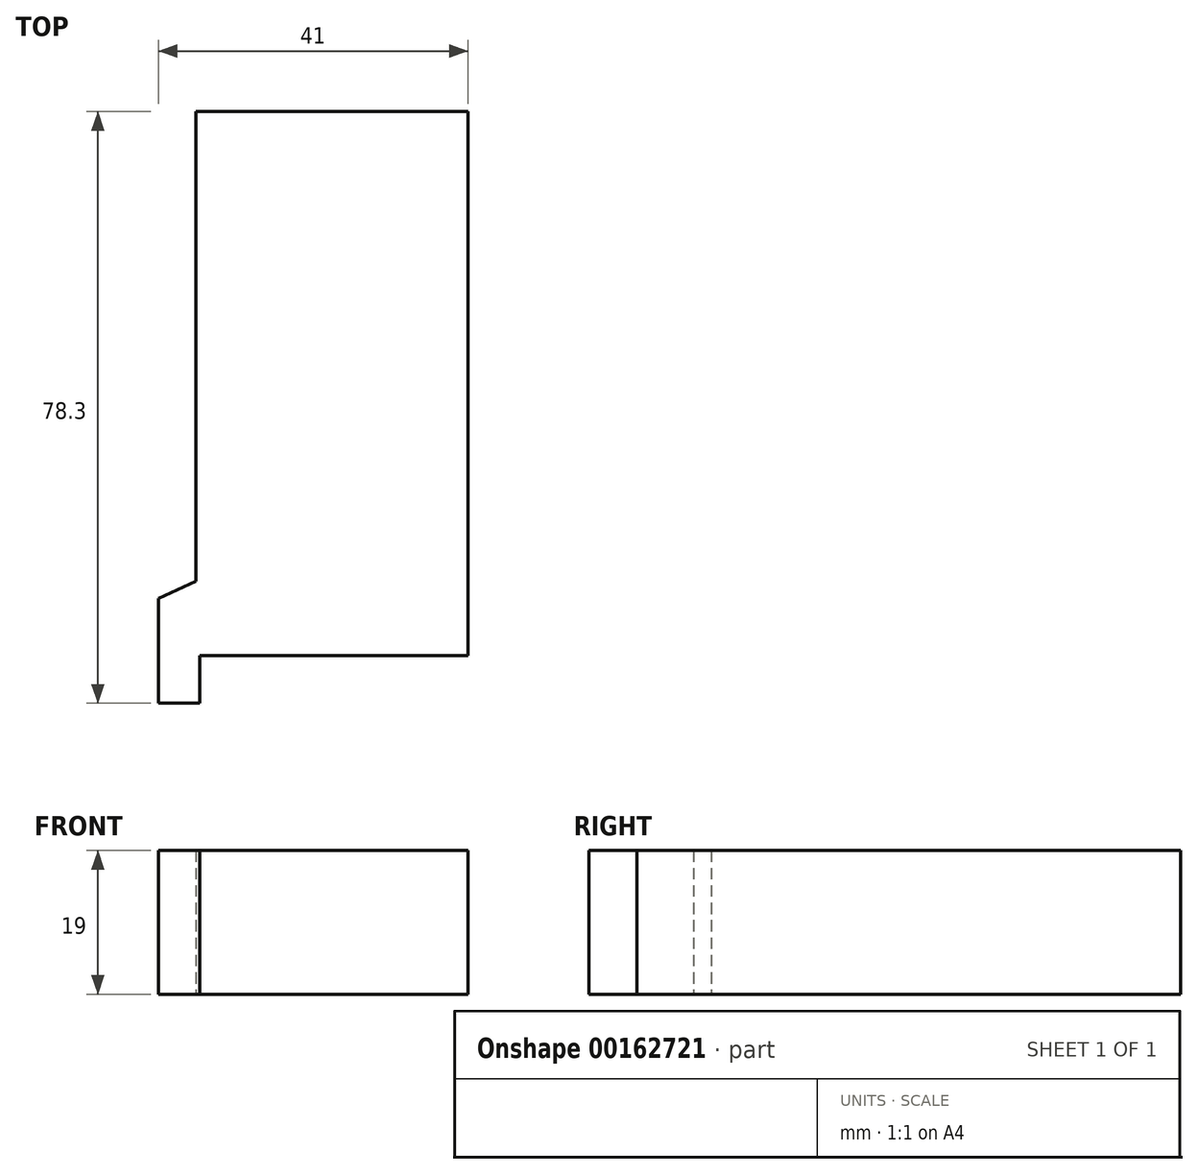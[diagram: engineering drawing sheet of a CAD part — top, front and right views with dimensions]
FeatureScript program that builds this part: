
annotation { "Feature Type Name" : "Feature", "Feature Type Description" : "" }
export const myFeature = defineFeature(function(context is Context, id is Id, definition is map)
    precondition{}
    {
        {
            var Q0;
            Q0=qCreatedBy(makeId("Top.planeOp"),FACE);
            var sketch = newSketch(context, id + "F0", { "sketchPlane" : qUnion([Q0])});
            skLineSegment(sketch, "E0.bottom", {"start": v(-18, 36) * mm, "end": v(18, 36) * mm});
            skLineSegment(sketch, "E0.top", {"start": v(-18, -36) * mm, "end": v(18, -36) * mm});
            skLineSegment(sketch, "E0.left", {"start": v(-18, 36) * mm, "end": v(-18, -36) * mm});
            skLineSegment(sketch, "E0.right", {"start": v(18, 36) * mm, "end": v(18, -36) * mm});
            skPoint(sketch, "E0.middle", {"position": v(0, 0) * mm});
            skLineSegment(sketch, "E1", {"start": v(-18, -26.12) * mm, "end": v(-23, -28.46) * mm});
            skLineSegment(sketch, "E2", {"start": v(-23, -28.46) * mm, "end": v(-23, -42.3) * mm});
            skLineSegment(sketch, "E3", {"start": v(-23, -42.3) * mm, "end": v(-17.54, -42.3) * mm});
            skLineSegment(sketch, "E4", {"start": v(-17.54, -42.3) * mm, "end": v(-17.54, -36) * mm});
            skSolve(sketch);
        }
        {
            var Q0;
            Q0=qSketchRegion(id+"F0",true);
            extrude(context, id + "F1", {"entities" : qUnion([Q0]), "depth" : 19 * mm});
        }
    });
